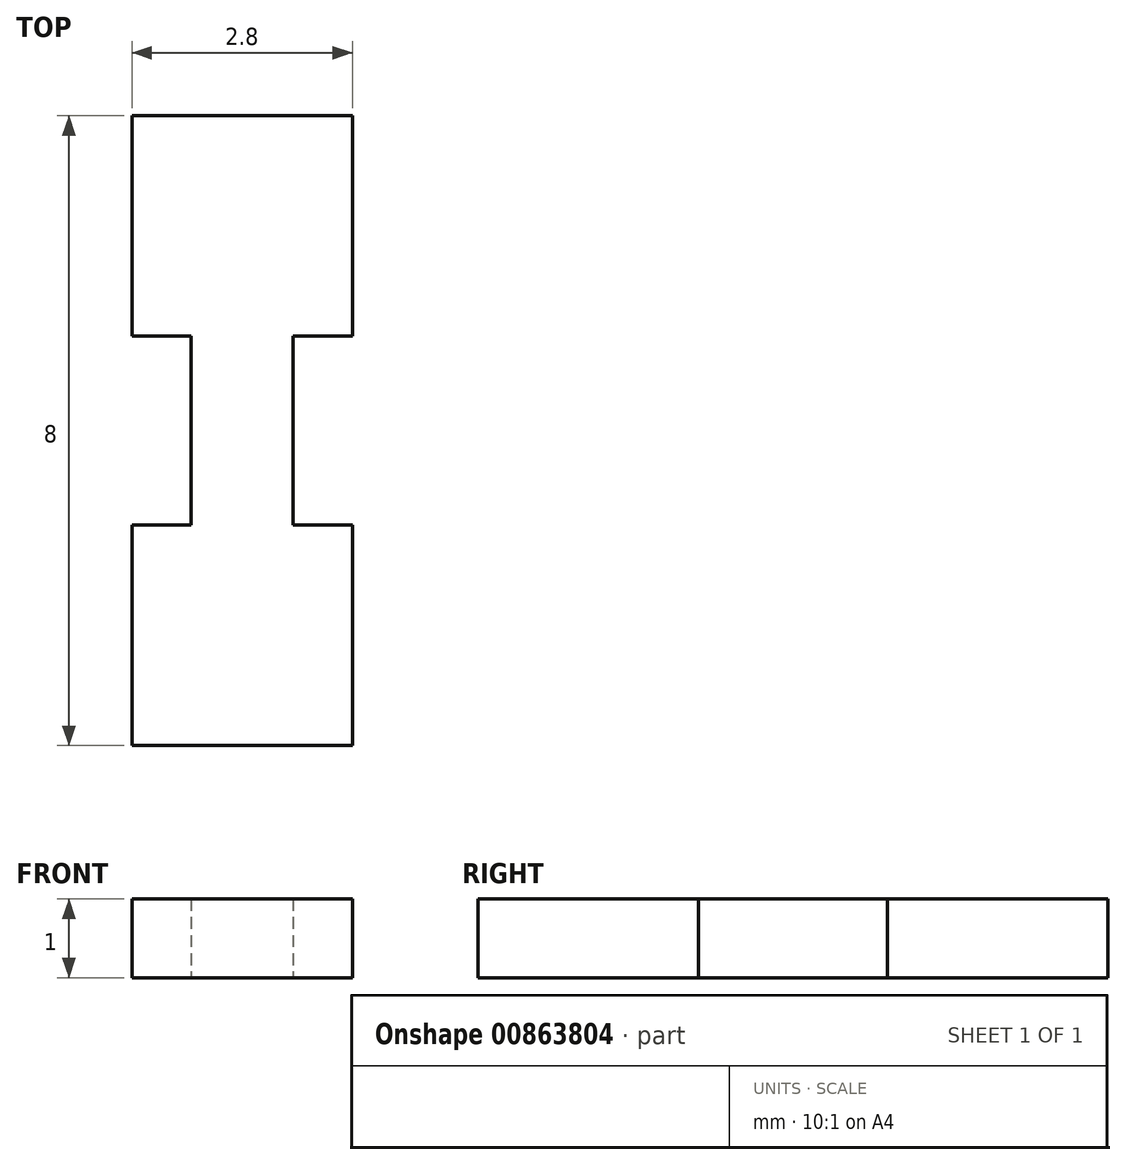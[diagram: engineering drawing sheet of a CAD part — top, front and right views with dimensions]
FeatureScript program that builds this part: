
annotation { "Feature Type Name" : "Feature", "Feature Type Description" : "" }
export const myFeature = defineFeature(function(context is Context, id is Id, definition is map)
    precondition{}
    {
        {
            var Q0;
            Q0=qCreatedBy(makeId("Top.planeOp"),FACE);
            var sketch = newSketch(context, id + "F0", { "sketchPlane" : qUnion([Q0])});
            skLineSegment(sketch, "E0.bottom", {"start": v(0, 0) * mm, "end": v(2.8, 0) * mm});
            skLineSegment(sketch, "E0.top", {"start": v(0, 8) * mm, "end": v(2.8, 8) * mm});
            skLineSegment(sketch, "E0.left", {"start": v(0, 0) * mm, "end": v(0, 8) * mm, "construction": true});
            skLineSegment(sketch, "E1", {"start": v(0, 5.2) * mm, "end": v(0.75, 5.2) * mm});
            skLineSegment(sketch, "E2", {"start": v(0.75, 5.2) * mm, "end": v(0.75, 2.8) * mm});
            skLineSegment(sketch, "E3", {"start": v(0.75, 2.8) * mm, "end": v(0, 2.8) * mm});
            skPoint(sketch, "E4", {"position": v(0.75, 4) * mm});
            skLineSegment(sketch, "E5", {"start": v(0.75, 4) * mm, "end": v(0, 4) * mm, "construction": true});
            skLineSegment(sketch, "E6", {"start": v(1.4, 8) * mm, "end": v(1.4, 0) * mm, "construction": true});
            skLineSegment(sketch, "E7", {"start": v(0, 8) * mm, "end": v(0, 5.2) * mm});
            skLineSegment(sketch, "E8", {"start": v(0, 2.8) * mm, "end": v(0, 0) * mm});
            skLineSegment(sketch, "E9.MirrorCS", {"start": v(2.05, 2.8) * mm, "end": v(2.8, 2.8) * mm});
            skLineSegment(sketch, "E10.MirrorCS", {"start": v(2.8, 5.2) * mm, "end": v(2.05, 5.2) * mm});
            skLineSegment(sketch, "E11.MirrorCS", {"start": v(2.05, 4) * mm, "end": v(2.8, 4) * mm, "construction": true});
            skPoint(sketch, "E12.MirrorP", {"position": v(2.05, 4) * mm});
            skLineSegment(sketch, "E13.MirrorCS", {"start": v(2.05, 5.2) * mm, "end": v(2.05, 2.8) * mm});
            skLineSegment(sketch, "E14.MirrorCS", {"start": v(2.8, 0) * mm, "end": v(2.8, 8) * mm, "construction": true});
            skLineSegment(sketch, "E15.MirrorCS", {"start": v(2.8, 8) * mm, "end": v(2.8, 5.2) * mm});
            skLineSegment(sketch, "E16.MirrorCS", {"start": v(2.8, 2.8) * mm, "end": v(2.8, 0) * mm});
            skSolve(sketch);
        }
        {
            var Q0;
            Q0=makeQuery(id+"F0.imprint","IMPRINT",FACE,{"disambiguationData":[TD([[makeQuery(id+"F0.imprint","IMPRINT",EDGE,{"derivedFrom":sQuery(id+"F0.wireOp",EDGE,"E0.bottom")}),1.0]])]});
            extrude(context, id + "F1", {"entities" : qUnion([Q0]), "depth" : 1 * mm, "offsetDistance" : 25 * mm});
        }
    });
